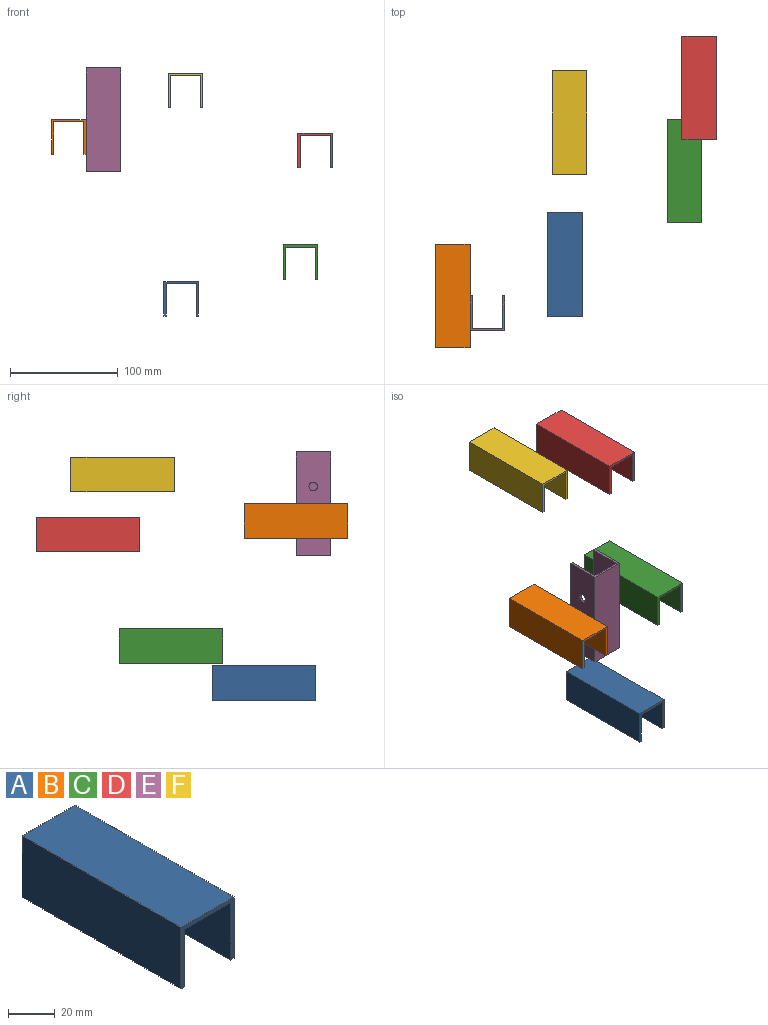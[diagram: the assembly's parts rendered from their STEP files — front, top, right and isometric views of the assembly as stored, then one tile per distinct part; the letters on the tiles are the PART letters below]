
ASSEMBLY  parts=6 mates=1
PART A: 12 faces, bbox 32x96x32 mm
  f0: plane 96x30mm, normal (1,0,0), area 2880mm2, adj f1,f7,f8,f10
  f1: plane 96x28mm, normal (0,0,-1), area 2688mm2, adj f0,f2,f8,f10
  f2: plane 96x30mm, normal (-1,0,0), area 2779.5mm2, adj f1,f3,f8,f9,f10,f11
  f3: plane 96x2mm, normal (0,0,-1), area 192mm2, adj f2,f4,f8,f10
  f4: plane 96x32mm, normal (1,0,0), area 2971.5mm2, adj f3,f5,f8,f9,f10,f11
  f5: plane 96x32mm, normal (0,0,1), area 3072mm2, adj f4,f6,f8,f10
  f6: plane 96x32mm, normal (-1,0,0), area 3072mm2, adj f5,f7,f8,f10
  f7: plane 96x2mm, normal (0,0,-1), area 192mm2, adj f0,f6,f8,f10
  f8: plane 32x32mm, normal (0,1,0), area 184mm2, adj f0,f1,f2,f3,f4,f5,f6,f7
  f9: cylinder r=4mm len=8mm, axis (1,0,0), area 50.3mm2, adj f2,f4
  f10: plane 32x32mm, normal (0,-1,0), area 184mm2, adj f0,f1,f2,f3,f4,f5,f6,f7
  f11: cylinder r=4mm len=8mm, axis (1,0,0), area 50.3mm2, adj f2,f4
PART B: same geometry as A
PART C: same geometry as A
PART D: same geometry as A
PART E: same geometry as A
PART F: same geometry as A
PLACE A t=(-16.26,-30.87,-102.07)mm
PLACE B rot(axis=(-0.25,0.28,0.93),0deg) t=(-120.51,-60.55,48.03)mm
PLACE C t=(94.32,55.65,-68.06)mm
PLACE D t=(108,132.48,35.33)mm
PLACE E rot(axis=(0,0.71,-0.71),180deg) t=(-56.51,-140.55,0.03)mm
PLACE F t=(-12.17,100.28,91.11)mm
MATE fastened E.f9 <-> B.f11  axis (-1,0,0) through (-88.51,-124.55,32.03)mm
